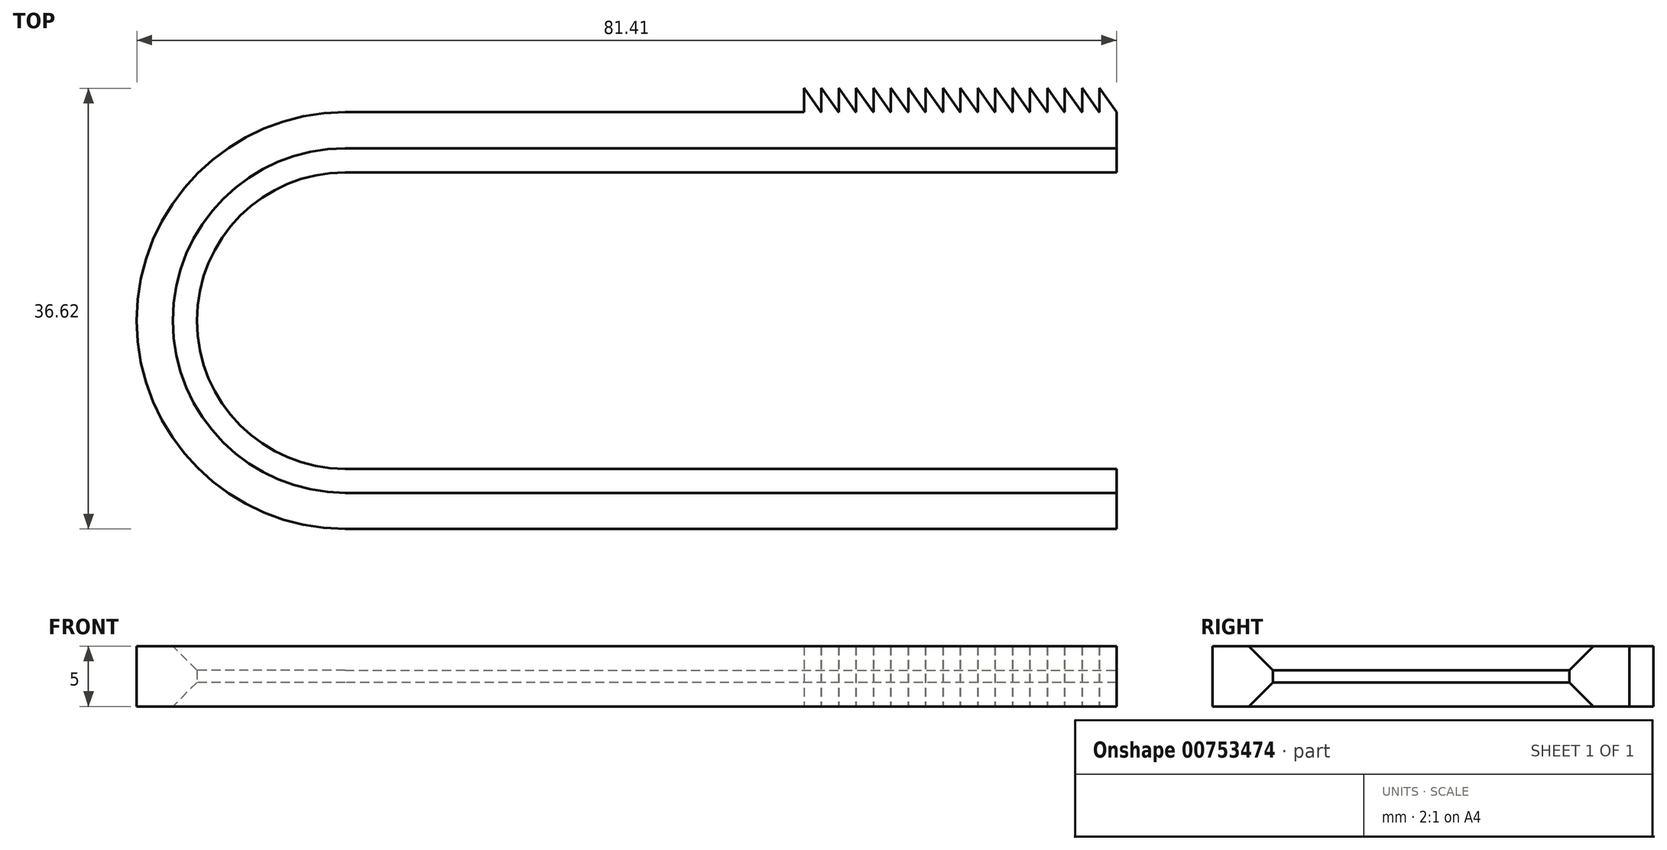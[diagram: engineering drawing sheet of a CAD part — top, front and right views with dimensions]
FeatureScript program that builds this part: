
annotation { "Feature Type Name" : "Feature", "Feature Type Description" : "" }
export const myFeature = defineFeature(function(context is Context, id is Id, definition is map)
    precondition{}
    {
        {
            var Q0;
            Q0=qCreatedBy(makeId("Top.planeOp"),FACE);
            var sketch = newSketch(context, id + "F0", { "sketchPlane" : qUnion([Q0])});
            skArc(sketch, "E0", {"start": v(-64.1, 12.31) * mm, "mid": v(-76.41, 0) * mm, "end": v(-64.1, -12.31) * mm});
            skArc(sketch, "E1", {"start": v(-64.1, 17.31) * mm, "mid": v(-81.41, 0) * mm, "end": v(-64.1, -17.31) * mm});
            skLineSegment(sketch, "E2", {"start": v(-64.1, 17.31) * mm, "end": v(0, 17.31) * mm});
            skLineSegment(sketch, "E3", {"start": v(0, 17.31) * mm, "end": v(0, 12.31) * mm});
            skLineSegment(sketch, "E4", {"start": v(0, 12.31) * mm, "end": v(-64.1, 12.31) * mm});
            skLineSegment(sketch, "E5", {"start": v(-64.1, -12.31) * mm, "end": v(0, -12.31) * mm});
            skLineSegment(sketch, "E6", {"start": v(0, -12.31) * mm, "end": v(0, -17.31) * mm});
            skLineSegment(sketch, "E7", {"start": v(0, -17.31) * mm, "end": v(-64.1, -17.31) * mm});
            skLineSegment(sketch, "E8", {"start": v(0, 17.31) * mm, "end": v(-1.42, 19.31) * mm});
            skLineSegment(sketch, "E9", {"start": v(-1.42, 19.31) * mm, "end": v(-1.42, 17.31) * mm});
            skLineSegment(sketch, "E10", {"start": v(-1.44, 17.31) * mm, "end": v(-2.86, 19.31) * mm});
            skLineSegment(sketch, "E11", {"start": v(-2.86, 19.31) * mm, "end": v(-2.86, 17.31) * mm});
            skLineSegment(sketch, "E12", {"start": v(-2.89, 17.31) * mm, "end": v(-4.3, 19.31) * mm});
            skLineSegment(sketch, "E13", {"start": v(-4.3, 19.31) * mm, "end": v(-4.3, 17.31) * mm});
            skLineSegment(sketch, "E14", {"start": v(-4.33, 17.31) * mm, "end": v(-5.75, 19.31) * mm});
            skLineSegment(sketch, "E15", {"start": v(-5.75, 19.31) * mm, "end": v(-5.75, 17.31) * mm});
            skLineSegment(sketch, "E16", {"start": v(-5.78, 17.31) * mm, "end": v(-7.2, 19.31) * mm});
            skLineSegment(sketch, "E17", {"start": v(-7.2, 19.31) * mm, "end": v(-7.2, 17.31) * mm});
            skLineSegment(sketch, "E18", {"start": v(-7.22, 17.31) * mm, "end": v(-8.64, 19.31) * mm});
            skLineSegment(sketch, "E19", {"start": v(-8.64, 19.31) * mm, "end": v(-8.64, 17.31) * mm});
            skLineSegment(sketch, "E20", {"start": v(-8.67, 17.31) * mm, "end": v(-10.08, 19.31) * mm});
            skLineSegment(sketch, "E21", {"start": v(-10.08, 19.31) * mm, "end": v(-10.08, 17.31) * mm});
            skLineSegment(sketch, "E22", {"start": v(-10.11, 17.31) * mm, "end": v(-11.53, 19.31) * mm});
            skLineSegment(sketch, "E23", {"start": v(-11.53, 19.31) * mm, "end": v(-11.53, 17.31) * mm});
            skLineSegment(sketch, "E24", {"start": v(-11.56, 17.31) * mm, "end": v(-12.97, 19.31) * mm});
            skLineSegment(sketch, "E25", {"start": v(-12.97, 19.31) * mm, "end": v(-12.97, 17.31) * mm});
            skLineSegment(sketch, "E26", {"start": v(-13, 17.31) * mm, "end": v(-14.42, 19.31) * mm});
            skLineSegment(sketch, "E27", {"start": v(-14.42, 19.31) * mm, "end": v(-14.42, 17.31) * mm});
            skLineSegment(sketch, "E28", {"start": v(-14.44, 17.31) * mm, "end": v(-15.86, 19.31) * mm});
            skLineSegment(sketch, "E29", {"start": v(-15.86, 19.31) * mm, "end": v(-15.86, 17.31) * mm});
            skLineSegment(sketch, "E30", {"start": v(-15.89, 17.31) * mm, "end": v(-17.3, 19.31) * mm});
            skLineSegment(sketch, "E31", {"start": v(-17.3, 19.31) * mm, "end": v(-17.3, 17.31) * mm});
            skLineSegment(sketch, "E32", {"start": v(-17.33, 17.31) * mm, "end": v(-18.75, 19.31) * mm});
            skLineSegment(sketch, "E33", {"start": v(-18.75, 19.31) * mm, "end": v(-18.75, 17.31) * mm});
            skLineSegment(sketch, "E34", {"start": v(-18.78, 17.31) * mm, "end": v(-20.2, 19.31) * mm});
            skLineSegment(sketch, "E35", {"start": v(-20.2, 19.31) * mm, "end": v(-20.2, 17.31) * mm});
            skLineSegment(sketch, "E36", {"start": v(-20.22, 17.31) * mm, "end": v(-21.64, 19.31) * mm});
            skLineSegment(sketch, "E37", {"start": v(-21.64, 19.31) * mm, "end": v(-21.64, 17.31) * mm});
            skLineSegment(sketch, "E38", {"start": v(-21.67, 17.31) * mm, "end": v(-23.08, 19.31) * mm});
            skLineSegment(sketch, "E39", {"start": v(-23.08, 19.31) * mm, "end": v(-23.08, 17.31) * mm});
            skLineSegment(sketch, "E40", {"start": v(-23.11, 17.31) * mm, "end": v(-24.53, 19.31) * mm});
            skLineSegment(sketch, "E41", {"start": v(-24.53, 19.31) * mm, "end": v(-24.53, 17.31) * mm});
            skLineSegment(sketch, "E42", {"start": v(-24.56, 17.31) * mm, "end": v(-25.97, 19.31) * mm});
            skLineSegment(sketch, "E43", {"start": v(-25.97, 19.31) * mm, "end": v(-25.97, 17.31) * mm});
            skSolve(sketch);
        }
        {
            var Q0;
            Q0=makeQuery(id+"F0.imprint","IMPRINT",FACE,{"disambiguationData":[TD([[makeQuery(id+"F0.imprint","IMPRINT",EDGE,{"derivedFrom":sQuery(id+"F0.wireOp",EDGE,"E0")}),-1.0]])]});
            var Q1;
            {var subQ0=sQuery(id+"F0.wireOp",EDGE,"E18");Q1=makeQuery(id+"F0.imprint","IMPRINT",FACE,{"disambiguationData":[TD([[makeQuery(id+"F0.imprint","IMPRINT",EDGE,{"derivedFrom":subQ0}),1.0]])]});}
            var Q2;
            {var subQ0=sQuery(id+"F0.wireOp",EDGE,"E22");Q2=makeQuery(id+"F0.imprint","IMPRINT",FACE,{"disambiguationData":[TD([[makeQuery(id+"F0.imprint","IMPRINT",EDGE,{"derivedFrom":subQ0}),1.0]])]});}
            var Q3;
            {var subQ0=sQuery(id+"F0.wireOp",EDGE,"E20");Q3=makeQuery(id+"F0.imprint","IMPRINT",FACE,{"disambiguationData":[TD([[makeQuery(id+"F0.imprint","IMPRINT",EDGE,{"derivedFrom":subQ0}),1.0]])]});}
            var Q4;
            {var subQ0=sQuery(id+"F0.wireOp",EDGE,"E24");Q4=makeQuery(id+"F0.imprint","IMPRINT",FACE,{"disambiguationData":[TD([[makeQuery(id+"F0.imprint","IMPRINT",EDGE,{"derivedFrom":subQ0}),1.0]])]});}
            var Q5;
            {var subQ0=sQuery(id+"F0.wireOp",EDGE,"E8");Q5=makeQuery(id+"F0.imprint","IMPRINT",FACE,{"disambiguationData":[TD([[makeQuery(id+"F0.imprint","IMPRINT",EDGE,{"derivedFrom":subQ0}),1.0]])]});}
            var Q6;
            {var subQ0=sQuery(id+"F0.wireOp",EDGE,"E36");Q6=makeQuery(id+"F0.imprint","IMPRINT",FACE,{"disambiguationData":[TD([[makeQuery(id+"F0.imprint","IMPRINT",EDGE,{"derivedFrom":subQ0}),1.0]])]});}
            var Q7;
            {var subQ0=sQuery(id+"F0.wireOp",EDGE,"E26");Q7=makeQuery(id+"F0.imprint","IMPRINT",FACE,{"disambiguationData":[TD([[makeQuery(id+"F0.imprint","IMPRINT",EDGE,{"derivedFrom":subQ0}),1.0]])]});}
            var Q8;
            {var subQ0=sQuery(id+"F0.wireOp",EDGE,"E16");Q8=makeQuery(id+"F0.imprint","IMPRINT",FACE,{"disambiguationData":[TD([[makeQuery(id+"F0.imprint","IMPRINT",EDGE,{"derivedFrom":subQ0}),1.0]])]});}
            var Q9;
            {var subQ0=sQuery(id+"F0.wireOp",EDGE,"E28");Q9=makeQuery(id+"F0.imprint","IMPRINT",FACE,{"disambiguationData":[TD([[makeQuery(id+"F0.imprint","IMPRINT",EDGE,{"derivedFrom":subQ0}),1.0]])]});}
            var Q10;
            {var subQ0=sQuery(id+"F0.wireOp",EDGE,"E30");Q10=makeQuery(id+"F0.imprint","IMPRINT",FACE,{"disambiguationData":[TD([[makeQuery(id+"F0.imprint","IMPRINT",EDGE,{"derivedFrom":subQ0}),1.0]])]});}
            var Q11;
            {var subQ0=sQuery(id+"F0.wireOp",EDGE,"E32");Q11=makeQuery(id+"F0.imprint","IMPRINT",FACE,{"disambiguationData":[TD([[makeQuery(id+"F0.imprint","IMPRINT",EDGE,{"derivedFrom":subQ0}),1.0]])]});}
            var Q12;
            {var subQ0=sQuery(id+"F0.wireOp",EDGE,"E34");Q12=makeQuery(id+"F0.imprint","IMPRINT",FACE,{"disambiguationData":[TD([[makeQuery(id+"F0.imprint","IMPRINT",EDGE,{"derivedFrom":subQ0}),1.0]])]});}
            var Q13;
            {var subQ0=sQuery(id+"F0.wireOp",EDGE,"E12");Q13=makeQuery(id+"F0.imprint","IMPRINT",FACE,{"disambiguationData":[TD([[makeQuery(id+"F0.imprint","IMPRINT",EDGE,{"derivedFrom":subQ0}),1.0]])]});}
            var Q14;
            {var subQ0=sQuery(id+"F0.wireOp",EDGE,"E38");Q14=makeQuery(id+"F0.imprint","IMPRINT",FACE,{"disambiguationData":[TD([[makeQuery(id+"F0.imprint","IMPRINT",EDGE,{"derivedFrom":subQ0}),1.0]])]});}
            var Q15;
            {var subQ0=sQuery(id+"F0.wireOp",EDGE,"E40");Q15=makeQuery(id+"F0.imprint","IMPRINT",FACE,{"disambiguationData":[TD([[makeQuery(id+"F0.imprint","IMPRINT",EDGE,{"derivedFrom":subQ0}),1.0]])]});}
            var Q16;
            {var subQ0=sQuery(id+"F0.wireOp",EDGE,"E42");Q16=makeQuery(id+"F0.imprint","IMPRINT",FACE,{"disambiguationData":[TD([[makeQuery(id+"F0.imprint","IMPRINT",EDGE,{"derivedFrom":subQ0}),1.0]])]});}
            var Q17;
            {var subQ0=sQuery(id+"F0.wireOp",EDGE,"E10");Q17=makeQuery(id+"F0.imprint","IMPRINT",FACE,{"disambiguationData":[TD([[makeQuery(id+"F0.imprint","IMPRINT",EDGE,{"derivedFrom":subQ0}),1.0]])]});}
            var Q18;
            {var subQ0=sQuery(id+"F0.wireOp",EDGE,"E14");Q18=makeQuery(id+"F0.imprint","IMPRINT",FACE,{"disambiguationData":[TD([[makeQuery(id+"F0.imprint","IMPRINT",EDGE,{"derivedFrom":subQ0}),1.0]])]});}
            extrude(context, id + "F1", {"entities" : qUnion([Q0, Q1, Q2, Q3, Q4, Q5, Q6, Q7, Q8, Q9, Q10, Q11, Q12, Q13, Q14, Q15, Q16, Q17, Q18]), "depth" : 5 * mm, "offsetDistance" : 25 * mm});
        }
        {
            var Q0;
            Q0=makeQuery(id+"F1.opExtrude","SWEPT_FACE",FACE,{"disambiguationData":[OSD([sQuery(id+"F0.wireOp",EDGE,"E0")])]});
            chamfer(context, id + "F2", {"entities" : qUnion([Q0]), "width" : 2 * mm, "tangentPropagation" : true});
        }
    });
